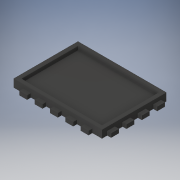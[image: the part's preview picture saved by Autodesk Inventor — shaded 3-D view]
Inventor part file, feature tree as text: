
AUTODESK INVENTOR PART (.ipt)
format: ipt  version: 2019 (Build 230136000, 136)  size: 224,768 bytes
history: native  units: mm
features: extrude x3, sketch x3, projected_geometry x1
ambient origin geometry x8: Origin, YZ Plane, XZ Plane, XY Plane, X Axis, Y Axis, Z Axis, Center Point
bodies: Solid1 (feature_tree)
feature tree (7):
  extrude  "Extrusion1"  Depth=75.0mm
  extrude  "Extrusion2"  Depth=4.0mm
  extrude  "Extrusion3"  Depth=4.0mm TaperAngle=0.0deg
  sketch  "Sketch1"  dims[d0=100.0mm d1=75.0mm]
  sketch  "Sketch2"  dims[d2=4.0mm d3=0.0mm d4=4.0mm]
  projected_geometry  "Projected Loop1"
  sketch  "Sketch3"  dims[d5=4.0mm d6=4.0mm d7=0.0mm d9=8.0mm d11=4.0mm d12=8.0mm d13=8.0mm d14=8.0mm d15=8.0mm d16=8.0mm d17=4.0mm d18=8.0mm d19=4.0mm d20=0.0mm]
